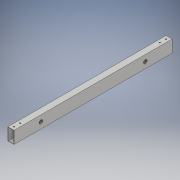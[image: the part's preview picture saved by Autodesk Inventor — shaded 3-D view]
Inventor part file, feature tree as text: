
AUTODESK INVENTOR PART (.ipt)
format: ipt  version: 2018 (Build 220112000, 112)  size: 133,120 bytes
history: native  units: in
note: dims shown in document units (in); Inventor stores cm internally (conversion verified against a paired STEP export)
features: extrude x3, sketch x3
ambient origin geometry x8: Origin, YZ Plane, XZ Plane, XY Plane, X Axis, Y Axis, Z Axis, Center Point
bodies: Solid1 (feature_tree)
feature tree (6):
  extrude  "Extrusion1"  Depth=2.0in
  extrude  "Extrusion2"  Depth=25.722in TaperAngle=0.0deg
  extrude  "Extrusion3"  Depth=1.0in
  sketch  "Sketch1"  dims[d0=1.0in d1=2.0in]
  sketch  "Sketch2"  dims[d2=0.0625in d3=25.722in d4=0.0in]
  sketch  "Sketch3"  dims[d5=0.5in d6=1.0in d7=0.5in d8=1.0in d9=0.2031in d10=25.722in d11=0.0in d12=4.361in d13=0.625in d14=25.722in d15=0.0in]
